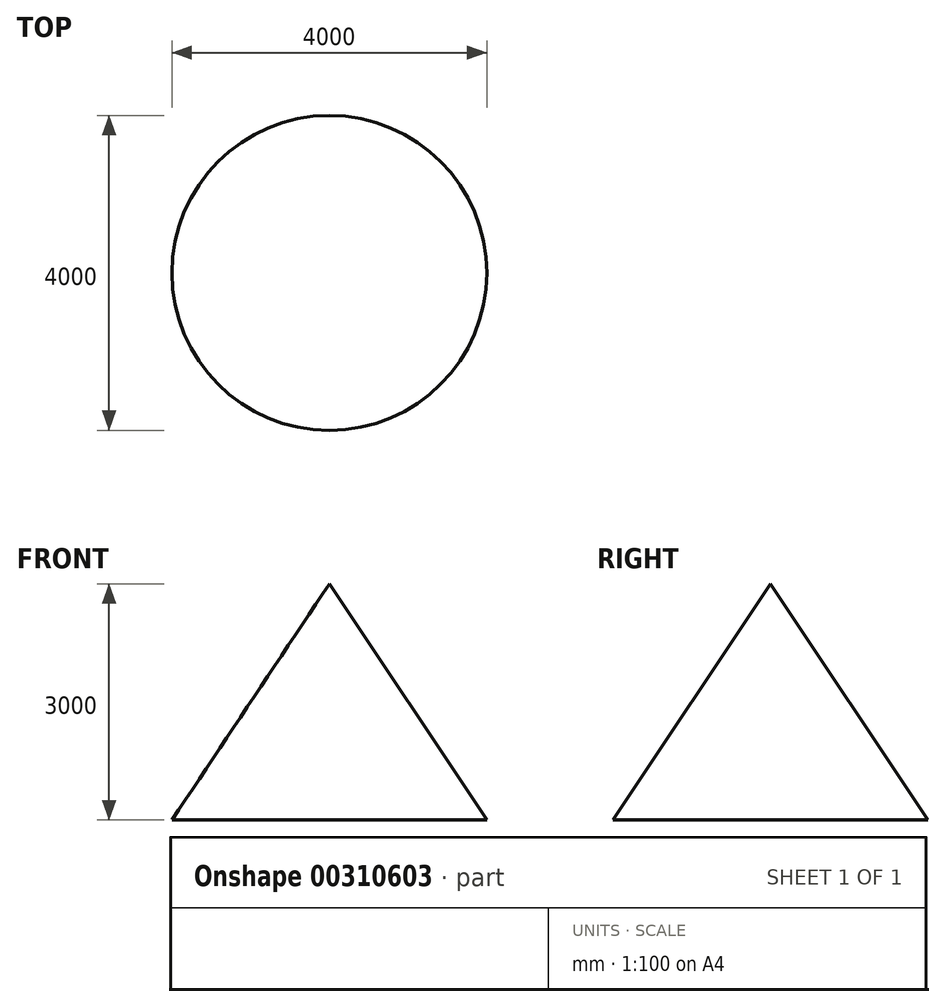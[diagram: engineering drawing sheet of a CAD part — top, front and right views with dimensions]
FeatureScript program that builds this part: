
annotation { "Feature Type Name" : "Feature", "Feature Type Description" : "" }
export const myFeature = defineFeature(function(context is Context, id is Id, definition is map)
    precondition{}
    {
        {
            var Q0;
            Q0=qCreatedBy(makeId("Front.planeOp"),FACE);
            var sketch = newSketch(context, id + "F0", { "sketchPlane" : qUnion([Q0])});
            skLineSegment(sketch, "E0", {"start": v(0, 0) * mm, "end": v(2000, 0) * mm});
            skLineSegment(sketch, "E1", {"start": v(2000, 0) * mm, "end": v(0, 3000) * mm});
            skLineSegment(sketch, "E2", {"start": v(0, 3000) * mm, "end": v(0, 0) * mm});
            skLineSegment(sketch, "E3", {"start": v(0, 3245.2) * mm, "end": v(0, -329.4) * mm, "construction": true});
            skSolve(sketch);
        }
        {
            var Q0;
            Q0 = qSketchRegion(id + "F0", true);
            var Q1;
            Q1=sQuery(id+"F0.wireOp",EDGE,"E3");
            revolve(context, id + "F1", {"entities" : qUnion([Q0]), "axis" : qUnion([Q1]), "revolveType" : RevolveType.FULL});
        }
    });
